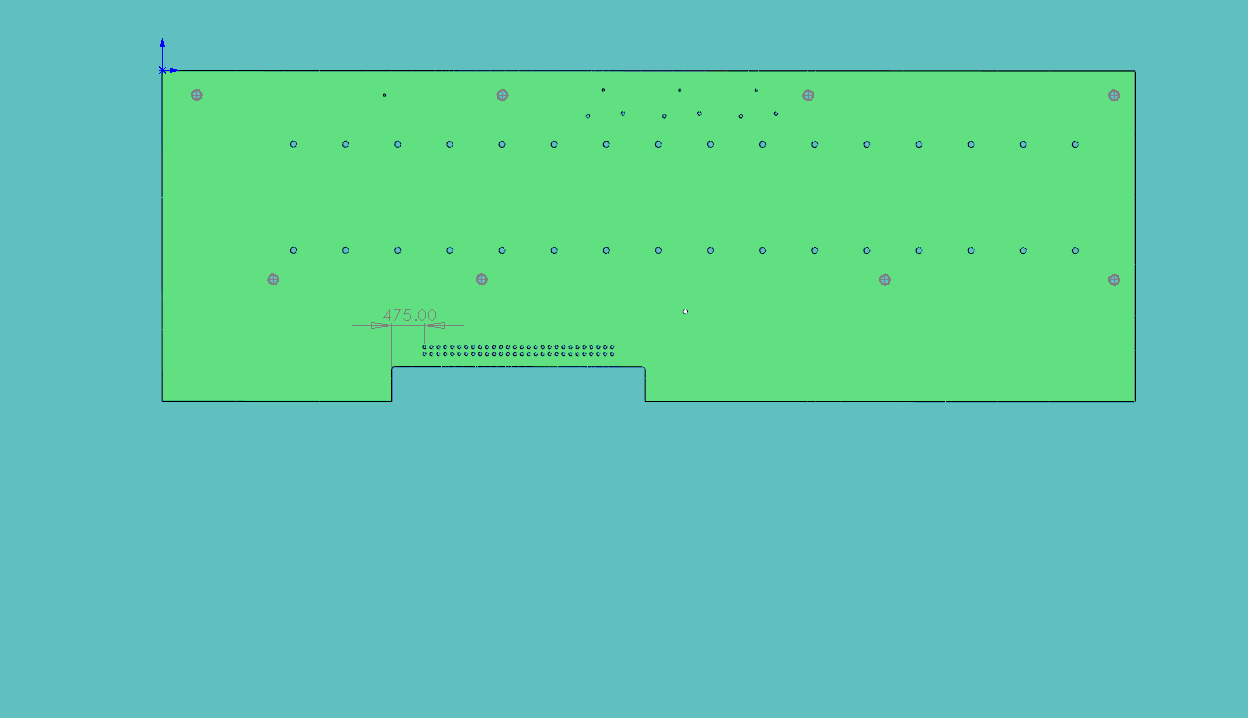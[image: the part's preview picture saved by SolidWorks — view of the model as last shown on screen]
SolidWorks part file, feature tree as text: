
SOLIDWORKS PART (.sldprt)
format: sldprt  version: not decoded by parser v0  size: 459,264 bytes
history: native  units: mm
features: sketch x8, cut_extrude x7, pattern_linear x3, material x1, extrude x1 + 1 further entry (+12 scaffold rows collapsed)
feature tree (33):
  "Annotations"  RD1=12.065mm
  scaffold x12  (default folders/planes/origin — collapsed)
  material  "Material <not specified>"
  sketch  "Sketch1"  dims[D1=120.65mm D2=355.6mm]
  extrude  "Extrude1"  Depth=1.5748mm
  sketch  "DSPboard connector holes"  dims[D1=2.3mm D4=2.3mm D2=55.118mm D3=48.006mm D5=38.73mm]
  cut_extrude  "Cut-Extrude1"  Depth=2.54mm
  pattern_linear  "LPattern1"  Count1=16 Count2=1 Spacing1=19.05mm Spacing2=50mm
  sketch  "Sketch2"  dims[D1=3.556mm D4=3.556mm D5=3.556mm D6=3.556mm D10=3.556mm D11=3.556mm D12=3.556mm D13=3.556mm D2=111.76mm D3=12.7mm D7=124.46mm D8=236.22mm D9=347.98mm D14=44.45mm D15=40.64mm D16=116.84mm D17=264.16mm D18=347.98mm]
  cut_extrude  "PCB Mount holes"  Depth=2.54mm
  sketch  "Sketch6"  dims[c1.D1=~1.35001mm c1.D2=~1.35001mm c1.D6=~1.35001mm c1.D7=~1.35001mm c1.D8=~1.35001mm c1.D9=~1.35001mm c1.D3=~14.240002mm c1.D4=1.0mm c1.D5=12.83mm c1.D10=~12.830048mm c1.D11=12.83mm c1.D12=~11.86401mm c1.D13=~10.535996mm c1.D14=~155.608325mm c2.D2=16.51mm]
  cut_extrude  "Peripheral-SATA"  Depth=2.54mm
  sketch  "Sketch7"  dims[c1.D1=~0.899998mm c1.D4=~0.899922mm c1.D5=~0.899922mm c1.D6=~0.899922mm c1.D2=4.826mm c1.D3=209.804mm c1.D7=4.826mm c1.D8=6.985mm c1.D9=8.89mm c1.D10=81.28mm c1.D11=161.29mm c1.D12=185.166mm c2.D2=27.94mm c2.D3=27.94mm]
  cut_extrude  "Off-board header holes"  Depth=2.54mm
  sketch  "Sketch9"  dims[D1=1.016mm D2=1.016mm D3=92.71mm D4=83.82mm D5=12.7mm]
  cut_extrude  "NIC cutout"  Depth=2.54mm
  sketch  "Sketch10"  dims[c1.D1=1.27mm c1.D2=21.082mm c1.D3=165.1mm c2.D2=7.112mm c2.D3=80.01mm c2.D4=12.7mm c3.D3=12.065mm]
  cut_extrude  "Header Holes"  Depth=2.54mm
  sketch  "BGA mount pos"  dims[D1=191.2mm D2=32.8mm]
  cut_extrude  "Cut-Extrude11"  Depth=0.254mm
  pattern_linear  "LPattern3"  Count1=28 Count2=2 Spacing1=2.54mm Spacing2=2.54mm
  pattern_linear  "LPattern4"  Count1=3 Count2=1 Spacing1=27.94mm Spacing2=50mm
decode coverage: 19 of 19 modeling features carry decoded parameters; 1 rows unclassified (native names shown)
note: ~ marks probable driven/reference dimensions
note: suppression state not decoded; provenance and decode notes live in map.json
